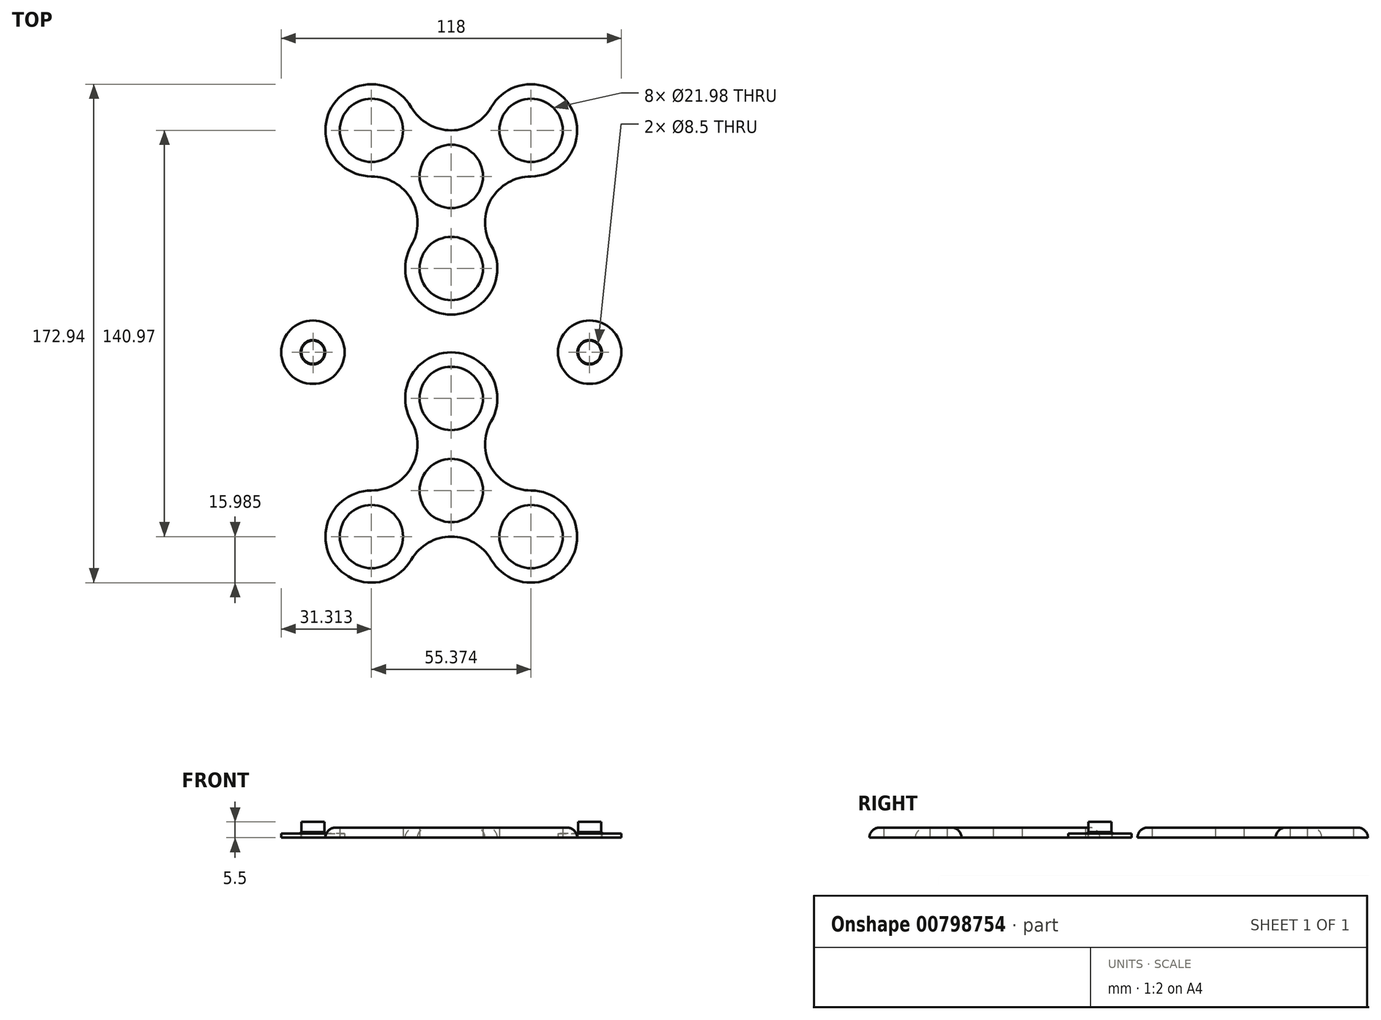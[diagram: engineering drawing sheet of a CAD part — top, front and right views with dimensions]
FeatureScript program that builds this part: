
annotation { "Feature Type Name" : "Feature", "Feature Type Description" : "" }
export const myFeature = defineFeature(function(context is Context, id is Id, definition is map)
    precondition{}
    {
        {
            var Q0;
            Q0=qCreatedBy(makeId("Top.planeOp"),FACE);
            var sketch = newSketch(context, id + "F0", { "sketchPlane" : qUnion([Q0])});
            skCircle(sketch, "E0", {"center": v(0, 0) * mm, "radius": 10.99 * mm});
            skCircle(sketch, "E1", {"center": v(27.69, -15.99) * mm, "radius": 10.99 * mm});
            skCircle(sketch, "E2", {"center": v(-27.69, -15.99) * mm, "radius": 10.99 * mm});
            skCircle(sketch, "E3", {"center": v(0, 31.97) * mm, "radius": 10.99 * mm});
            skPoint(sketch, "E4", {"position": v(-13.84, 8) * mm});
            skPoint(sketch, "E5", {"position": v(13.84, 8) * mm});
            skPoint(sketch, "E6", {"position": v(0, -15.99) * mm});
            skArc(sketch, "E7", {"start": v(0, -15.99) * mm, "mid": v(-8, -18.13) * mm, "end": v(-13.84, -23.98) * mm});
            skArc(sketch, "E8", {"start": v(13.84, -23.98) * mm, "mid": v(8, -18.13) * mm, "end": v(0, -15.99) * mm});
            skArc(sketch, "E9", {"start": v(13.84, 8) * mm, "mid": v(19.7, 2.14) * mm, "end": v(27.69, 0) * mm});
            skArc(sketch, "E10", {"start": v(13.84, 23.98) * mm, "mid": v(11.7, 15.99) * mm, "end": v(13.84, 8) * mm});
            skArc(sketch, "E11", {"start": v(-13.84, 8) * mm, "mid": v(-11.7, 15.99) * mm, "end": v(-13.84, 23.98) * mm});
            skArc(sketch, "E12", {"start": v(-27.69, 0) * mm, "mid": v(-19.7, 2.14) * mm, "end": v(-13.84, 8) * mm});
            skArc(sketch, "E13", {"start": v(13.84, 23.98) * mm, "mid": v(0, 47.96) * mm, "end": v(-13.84, 23.98) * mm});
            skArc(sketch, "E14", {"start": v(-27.69, 0) * mm, "mid": v(-41.53, -23.98) * mm, "end": v(-13.84, -23.98) * mm});
            skArc(sketch, "E15", {"start": v(13.84, -23.98) * mm, "mid": v(41.53, -23.98) * mm, "end": v(27.69, 0) * mm});
            skSolve(sketch);
        }
        {
            var Q0;
            Q0=makeQuery(id+"F0.imprint","IMPRINT",FACE,{"disambiguationData":[TD([[makeQuery(id+"F0.imprint","IMPRINT",EDGE,{"derivedFrom":sQuery(id+"F0.wireOp",EDGE,"E0")}),-1.0]])]});
            extrude(context, id + "F1", {"entities" : qUnion([Q0]), "depth" : (7 / 2) * mm, "offsetDistance" : 25 * mm});
        }
        {
            var Q0;
            Q0=makeQuery(id+"F1.opExtrude","CAP_EDGE",EDGE,{"disambiguationData":[OSD([sQuery(id+"F0.wireOp",EDGE,"E14")])],"isStart":false});
            fillet(context, id + "F2", {"entities" : qUnion([Q0]), "radius" : 3.5 * mm, "tangentPropagation" : true, "allowEdgeOverflow" : false});
        }
        {
            var Q0;
            Q0=qCreatedBy(makeId("Top.planeOp"),FACE);
            var sketch = newSketch(context, id + "F3", { "sketchPlane" : qUnion([Q0])});
            skCircle(sketch, "E16", {"center": v(-48, 48) * mm, "radius": 11 * mm});
            skCircle(sketch, "E17", {"center": v(48, 48) * mm, "radius": 11 * mm});
            skCircle(sketch, "E18", {"center": v(-48, 48) * mm, "radius": 4.25 * mm});
            skCircle(sketch, "E19", {"center": v(48, 48) * mm, "radius": 4.25 * mm});
            skCircle(sketch, "E20", {"center": v(-48, 48) * mm, "radius": 4 * mm});
            skCircle(sketch, "E21", {"center": v(48, 48) * mm, "radius": 4 * mm});
            skSolve(sketch);
        }
        {
            var Q0;
            {var subQ0=sQuery(id+"F3.wireOp",EDGE,"E16");var subQ1=sQuery(id+"F3.wireOp",EDGE,"PVz9Oi85-gcZB-t3ZF-1mhl-ecHQKdnhl3ld.top");var subQ2=makeQuery(id+"F3.imprint","INTERSECT",VERTEX,{"derivedFrom":[subQ1,subQ0]});Q0=makeQuery(id+"F3.imprint","IMPRINT",FACE,{"disambiguationData":[TD([[makeQuery(id+"F3.imprint","IMPRINT",EDGE,{"disambiguationData":[TD([[subQ2,-1.0]])],"derivedFrom":subQ1}),-1.0]])]});}
            var Q1;
            {var subQ0=sQuery(id+"F3.wireOp",EDGE,"E17");var subQ1=sQuery(id+"F3.wireOp",EDGE,"4iMSizte-IEy9-JDpa-06AD-8ywAavxXxgop.top");var subQ2=makeQuery(id+"F3.imprint","INTERSECT",VERTEX,{"derivedFrom":[subQ1,subQ0]});Q1=makeQuery(id+"F3.imprint","IMPRINT",FACE,{"disambiguationData":[TD([[makeQuery(id+"F3.imprint","IMPRINT",EDGE,{"disambiguationData":[TD([[subQ2,-1.0]])],"derivedFrom":subQ1}),1.0]])]});}
            var Q2;
            {var subQ0=sQuery(id+"F3.wireOp",EDGE,"E17");var subQ1=sQuery(id+"F3.wireOp",EDGE,"4iMSizte-IEy9-JDpa-06AD-8ywAavxXxgop.top");var subQ2=makeQuery(id+"F3.imprint","INTERSECT",VERTEX,{"derivedFrom":[subQ1,subQ0]});Q2=makeQuery(id+"F3.imprint","IMPRINT",FACE,{"disambiguationData":[TD([[makeQuery(id+"F3.imprint","IMPRINT",EDGE,{"disambiguationData":[TD([[subQ2,-1.0]])],"derivedFrom":subQ1}),-1.0]])]});}
            var Q3;
            {var subQ0=sQuery(id+"F3.wireOp",EDGE,"E16");var subQ1=sQuery(id+"F3.wireOp",EDGE,"PVz9Oi85-gcZB-t3ZF-1mhl-ecHQKdnhl3ld.top");var subQ2=makeQuery(id+"F3.imprint","INTERSECT",VERTEX,{"derivedFrom":[subQ1,subQ0]});Q3=makeQuery(id+"F3.imprint","IMPRINT",FACE,{"disambiguationData":[TD([[makeQuery(id+"F3.imprint","IMPRINT",EDGE,{"disambiguationData":[TD([[subQ2,-1.0]])],"derivedFrom":subQ1}),1.0]])]});}
            var Q4;
            Q4=makeQuery(id+"F3.imprint","IMPRINT",FACE,{"disambiguationData":[TD([[makeQuery(id+"F3.imprint","IMPRINT",EDGE,{"derivedFrom":sQuery(id+"F3.wireOp",EDGE,"E16")}),1.0]])]});
            var Q5;
            Q5=makeQuery(id+"F3.imprint","IMPRINT",FACE,{"disambiguationData":[TD([[makeQuery(id+"F3.imprint","IMPRINT",EDGE,{"derivedFrom":sQuery(id+"F3.wireOp",EDGE,"E17")}),1.0]])]});
            extrude(context, id + "F4", {"entities" : qUnion([Q0, Q1, Q2, Q3, Q4, Q5]), "depth" : 1.5 * mm, "offsetDistance" : 25 * mm});
        }
        {
            var Q0;
            {var subQ0=sQuery(id+"F3.wireOp",EDGE,"E18");var subQ1=sQuery(id+"F3.wireOp",EDGE,"PVz9Oi85-gcZB-t3ZF-1mhl-ecHQKdnhl3ld.top");var subQ2=makeQuery(id+"F3.imprint","INTERSECT",VERTEX,{"derivedFrom":[subQ1,subQ0]});Q0=makeQuery(id+"F3.imprint","IMPRINT",FACE,{"disambiguationData":[TD([[makeQuery(id+"F3.imprint","IMPRINT",EDGE,{"disambiguationData":[TD([[subQ2,-1.0]])],"derivedFrom":subQ1}),-1.0]])]});}
            var Q1;
            {var subQ0=sQuery(id+"F3.wireOp",EDGE,"E18");var subQ1=sQuery(id+"F3.wireOp",EDGE,"PVz9Oi85-gcZB-t3ZF-1mhl-ecHQKdnhl3ld.top");var subQ2=makeQuery(id+"F3.imprint","INTERSECT",VERTEX,{"derivedFrom":[subQ1,subQ0]});Q1=makeQuery(id+"F3.imprint","IMPRINT",FACE,{"disambiguationData":[TD([[makeQuery(id+"F3.imprint","IMPRINT",EDGE,{"disambiguationData":[TD([[subQ2,-1.0]])],"derivedFrom":subQ1}),1.0]])]});}
            var Q2;
            {var subQ0=sQuery(id+"F3.wireOp",EDGE,"E19");var subQ1=sQuery(id+"F3.wireOp",EDGE,"4iMSizte-IEy9-JDpa-06AD-8ywAavxXxgop.top");var subQ2=makeQuery(id+"F3.imprint","INTERSECT",VERTEX,{"derivedFrom":[subQ1,subQ0]});Q2=makeQuery(id+"F3.imprint","IMPRINT",FACE,{"disambiguationData":[TD([[makeQuery(id+"F3.imprint","IMPRINT",EDGE,{"disambiguationData":[TD([[subQ2,-1.0]])],"derivedFrom":subQ1}),1.0]])]});}
            var Q3;
            {var subQ0=sQuery(id+"F3.wireOp",EDGE,"E19");var subQ1=sQuery(id+"F3.wireOp",EDGE,"4iMSizte-IEy9-JDpa-06AD-8ywAavxXxgop.top");var subQ2=makeQuery(id+"F3.imprint","INTERSECT",VERTEX,{"derivedFrom":[subQ1,subQ0]});Q3=makeQuery(id+"F3.imprint","IMPRINT",FACE,{"disambiguationData":[TD([[makeQuery(id+"F3.imprint","IMPRINT",EDGE,{"disambiguationData":[TD([[subQ2,-1.0]])],"derivedFrom":subQ1}),-1.0]])]});}
            var Q4;
            Q4=makeQuery(id+"F3.imprint","IMPRINT",FACE,{"disambiguationData":[TD([[makeQuery(id+"F3.imprint","IMPRINT",EDGE,{"derivedFrom":sQuery(id+"F3.wireOp",EDGE,"E18")}),1.0]])]});
            var Q5;
            Q5=makeQuery(id+"F3.imprint","IMPRINT",FACE,{"disambiguationData":[TD([[makeQuery(id+"F3.imprint","IMPRINT",EDGE,{"derivedFrom":sQuery(id+"F3.wireOp",EDGE,"E19")}),1.0]])]});
            extrude(context, id + "F5", {"entities" : qUnion([Q0, Q1, Q2, Q3, Q4, Q5]), "depth" : 2 * mm, "offsetDistance" : 25 * mm});
        }
        {
            var Q0;
            {var subQ0=sQuery(id+"F3.wireOp",EDGE,"PVz9Oi85-gcZB-t3ZF-1mhl-ecHQKdnhl3ld.right");var subQ1=sQuery(id+"F3.wireOp",EDGE,"PVz9Oi85-gcZB-t3ZF-1mhl-ecHQKdnhl3ld.top");var subQ2=makeQuery(id+"F3.imprint","INTERSECT",VERTEX,{"derivedFrom":[subQ1,subQ0]});Q0=makeQuery(id+"F3.imprint","IMPRINT",FACE,{"disambiguationData":[TD([[makeQuery(id+"F3.imprint","IMPRINT",EDGE,{"disambiguationData":[TD([[subQ2,1.0]])],"derivedFrom":subQ1}),-1.0]])]});}
            var Q1;
            {var subQ0=sQuery(id+"F3.wireOp",EDGE,"PVz9Oi85-gcZB-t3ZF-1mhl-ecHQKdnhl3ld.right");var subQ1=sQuery(id+"F3.wireOp",EDGE,"PVz9Oi85-gcZB-t3ZF-1mhl-ecHQKdnhl3ld.top");var subQ2=makeQuery(id+"F3.imprint","INTERSECT",VERTEX,{"derivedFrom":[subQ1,subQ0]});Q1=makeQuery(id+"F3.imprint","IMPRINT",FACE,{"disambiguationData":[TD([[makeQuery(id+"F3.imprint","IMPRINT",EDGE,{"disambiguationData":[TD([[subQ2,1.0]])],"derivedFrom":subQ1}),1.0]])]});}
            var Q2;
            {var subQ0=sQuery(id+"F3.wireOp",EDGE,"4iMSizte-IEy9-JDpa-06AD-8ywAavxXxgop.right");var subQ1=sQuery(id+"F3.wireOp",EDGE,"4iMSizte-IEy9-JDpa-06AD-8ywAavxXxgop.top");var subQ2=makeQuery(id+"F3.imprint","INTERSECT",VERTEX,{"derivedFrom":[subQ1,subQ0]});Q2=makeQuery(id+"F3.imprint","IMPRINT",FACE,{"disambiguationData":[TD([[makeQuery(id+"F3.imprint","IMPRINT",EDGE,{"disambiguationData":[TD([[subQ2,1.0]])],"derivedFrom":subQ1}),1.0]])]});}
            var Q3;
            {var subQ0=sQuery(id+"F3.wireOp",EDGE,"4iMSizte-IEy9-JDpa-06AD-8ywAavxXxgop.right");var subQ1=sQuery(id+"F3.wireOp",EDGE,"4iMSizte-IEy9-JDpa-06AD-8ywAavxXxgop.top");var subQ2=makeQuery(id+"F3.imprint","INTERSECT",VERTEX,{"derivedFrom":[subQ1,subQ0]});Q3=makeQuery(id+"F3.imprint","IMPRINT",FACE,{"disambiguationData":[TD([[makeQuery(id+"F3.imprint","IMPRINT",EDGE,{"disambiguationData":[TD([[subQ2,1.0]])],"derivedFrom":subQ1}),-1.0]])]});}
            var Q4;
            Q4=makeQuery(id+"F3.imprint","IMPRINT",FACE,{"disambiguationData":[TD([[makeQuery(id+"F3.imprint","IMPRINT",EDGE,{"derivedFrom":sQuery(id+"F3.wireOp",EDGE,"E20")}),1.0]])]});
            var Q5;
            Q5=makeQuery(id+"F3.imprint","IMPRINT",FACE,{"disambiguationData":[TD([[makeQuery(id+"F3.imprint","IMPRINT",EDGE,{"derivedFrom":sQuery(id+"F3.wireOp",EDGE,"E21")}),1.0]])]});
            extrude(context, id + "F6", {"entities" : qUnion([Q0, Q1, Q2, Q3, Q4, Q5]), "depth" : 5.5 * mm, "offsetDistance" : 25 * mm});
        }
        {
            var Q0;
            Q0=makeQuery(id+"F1.opExtrude","SWEPT_BODY",BODY,{"disambiguationData":[OSD([sQuery(id+"F0.wireOp",EDGE,"E0"),sQuery(id+"F0.wireOp",EDGE,"E1"),sQuery(id+"F0.wireOp",EDGE,"E2"),sQuery(id+"F0.wireOp",EDGE,"E3"),sQuery(id+"F0.wireOp",EDGE,"E7"),sQuery(id+"F0.wireOp",EDGE,"E8"),sQuery(id+"F0.wireOp",EDGE,"E9"),sQuery(id+"F0.wireOp",EDGE,"E10"),sQuery(id+"F0.wireOp",EDGE,"E11"),sQuery(id+"F0.wireOp",EDGE,"E12"),sQuery(id+"F0.wireOp",EDGE,"E13"),sQuery(id+"F0.wireOp",EDGE,"E14"),sQuery(id+"F0.wireOp",EDGE,"E15")])]});
            var Q1;
            Q1=qCreatedBy(makeId("Front.planeOp"),FACE);
            mirror(context, id + "F7", {"entities" : qUnion([Q0]), "mirrorPlane" : qUnion([Q1])});
        }
        {
            var Q0;
            Q0=makeQuery(id+"F7.opPattern","COPY",BODY,{"derivedFrom":makeQuery(id+"F1.opExtrude","SWEPT_BODY",BODY,{"disambiguationData":[OSD([sQuery(id+"F0.wireOp",EDGE,"E0"),sQuery(id+"F0.wireOp",EDGE,"E1"),sQuery(id+"F0.wireOp",EDGE,"E2"),sQuery(id+"F0.wireOp",EDGE,"E3"),sQuery(id+"F0.wireOp",EDGE,"E7"),sQuery(id+"F0.wireOp",EDGE,"E8"),sQuery(id+"F0.wireOp",EDGE,"E9"),sQuery(id+"F0.wireOp",EDGE,"E10"),sQuery(id+"F0.wireOp",EDGE,"E11"),sQuery(id+"F0.wireOp",EDGE,"E12"),sQuery(id+"F0.wireOp",EDGE,"E13"),sQuery(id+"F0.wireOp",EDGE,"E14"),sQuery(id+"F0.wireOp",EDGE,"E15")])]}),"instanceName":"1"});
            var Q1;
            Q1=qCreatedBy(makeId("Front.planeOp"),FACE);
            transform(context, id + "F8", {"entities" : qUnion([Q0]), "transformType" : TransformType.TRANSLATION_DISTANCE, "transformDirection" : qUnion([Q1]), "distance" : 109 * mm, "oppositeDirection" : true, "makeCopy" : false});
        }
    });
